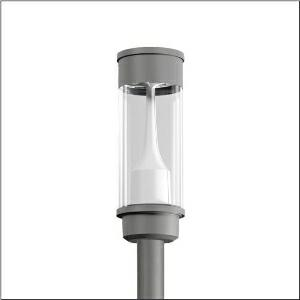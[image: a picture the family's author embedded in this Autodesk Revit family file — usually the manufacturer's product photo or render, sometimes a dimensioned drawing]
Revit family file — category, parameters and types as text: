
# Revit family: litepole_iq___st1_2a_5xa5415mf14h_d5a4
name_source: partatom
category: Lighting Fixtures
units: mm (PartAtom-declared; Revit-internal decimal feet)

## family parameters
Cut with Voids When Loaded = No
Host = Face
Light Source = No
Part Type = Normal
Room Calculation Point = No
Round Connector Dimension = Use Diameter
Shared = No

## types (1)
- --- (1 x LED, 1540 lm, 11.8 W, 2700K)
    Apparent Load = 12 VA
    CIE Flux Codes = 22 61 93 96 100
    Color Rendering = 70
    Color Temperature = 2700K
    Default Elevation = 1800 mm
    Description = Litepole iQ, mast luminaire, Module 540 iQ-SR, primary light control with 3 zone facetted reflector, of plastic, silver coated, highly specular, structured, primary optical cover: cover, of PMMA, transparent, partly coated, light distribution: ST1.2a, light emission: direct distribution, primary light characteristic: asymmetric, installation type: post-top, LED, High Power LED, rated luminous flux: 1.540lm, luminous efficacy: 131lm/W, light colour: 727, colour temperature: 2700K, control gear: ECG iQ, control: optimised constant luminous flux control (CLO 2.0), Desk-Remote (wireless, voltage-free reading and setting of iQ features in the workshop via application-optimized NFC function/RFID function), Light-Fading, Smart-Wire, Night-Set, Lumen-Switch, Temp-Guard, Auto-Match, Street-Remote, presetting dimming logarithmic, with terminal, 6-pole, max. 2.5mm², mains connection: 220..240V, AC, 50/60Hz, start of lifetime: 12W, end of lifetime: 12W, reduction: 6W, luminaire housing, upper part, of glass-fibre reinforced polyester, coated, Siteco® metallic grey (DB 702S), diameter: 210mm, height: 590mm, spigot size: d x l = 76 x 70mm (post-top) | with reducer (optional accessory) 60 x 70mm, post-top mast mounting element, of diecast aluminium, coated, Siteco® metallic grey (DB 702S), Module 540 iQ-SR, traffic white (RAL 9016), equipment: standard, protection rating (complete): IP65, insulation class (complete): insulation class II (safety insulation), certification: CE, ENEC, VDE, packaging unit: 1 piece

Light Distribution: ST1.2a
    Height = 590 mm
    Lamp = 1 x LED
    Lamp Light Flux = 1540 lm
    Lamp Power = 11.8 W
    Lamp count = 1
    Length = 220 mm
    Luminous efficacy = 131 lm/W
    Manufacturer = Siteco
    ModVariant = No
    Model = 5XA5415MF14H
    Number of Poles = 1
    OnlyDefault = Yes
    Power Factor = 1
    Product Name = Litepole iQ | ST1.2a
    Product group = mast luminaire | pylon top
    ProductGroupID = 6100
    Protection Class = Protection class II
    Protection Degree = IP 65
    RLX_Detail_Level = 1
    RlxData = <blob elided: 71821 chars, md5=803c4f16>
    Socket = socket
    Standby Power = 0 W
    System Light Flux = 1540 lm
    System Power = 12 W
    Type Comments = factory setting: luminous flux: 100 % | dim-lin: 254 | 472 mA
    Type Image = l_1006025.jpg
    URL = http://relux.com
    VarID = @adj_062865
    Voltage = 0 V
    Weight = 0.00 kg
    Width = 0 mm  [stored 0 ft]

note: [stored X ft] marks values corroborated as IEEE doubles in the binary element streams (Revit-internal decimal feet)

## geometry (parser evidence)
native form markers: Blend x4, Sweep x10
no freeform markers — native parametric forms only
